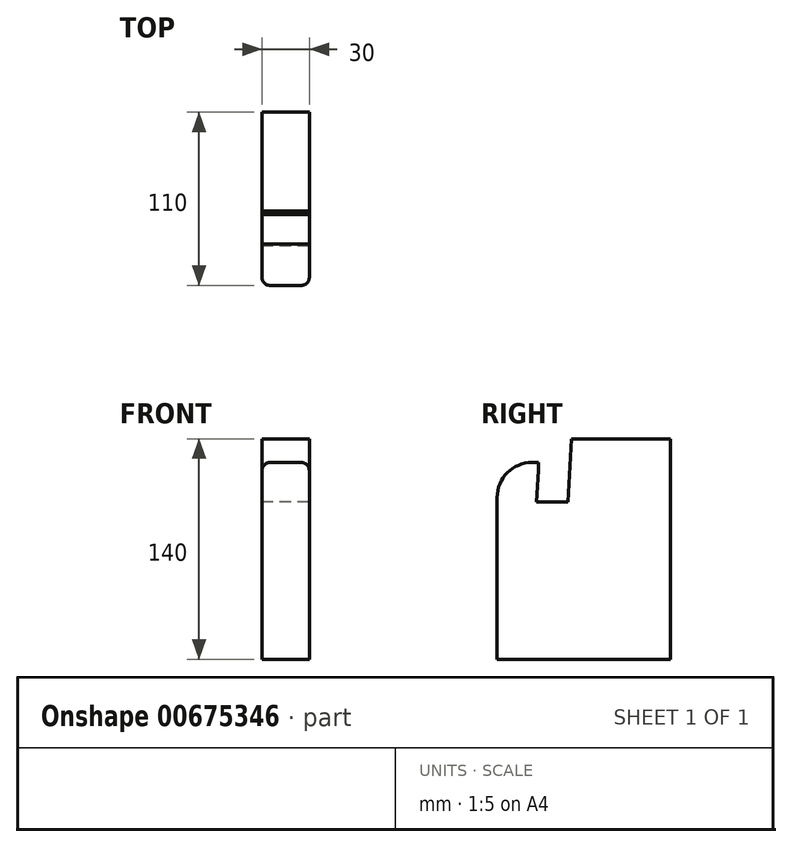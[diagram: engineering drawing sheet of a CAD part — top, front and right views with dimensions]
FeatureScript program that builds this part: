
annotation { "Feature Type Name" : "Feature", "Feature Type Description" : "" }
export const myFeature = defineFeature(function(context is Context, id is Id, definition is map)
    precondition{}
    {
        {
            var Q0;
            Q0=qCreatedBy(makeId("Right.planeOp"),FACE);
            var sketch = newSketch(context, id + "F0", { "sketchPlane" : qUnion([Q0])});
            skLineSegment(sketch, "E0", {"start": v(0, 0) * mm, "end": v(2.1, 39.95) * mm});
            skLineSegment(sketch, "E1", {"start": v(-20, 0) * mm, "end": v(-18.7, 24.97) * mm});
            skLineSegment(sketch, "E2", {"start": v(0, 0) * mm, "end": v(29.88, 570.22) * mm, "construction": true});
            skLineSegment(sketch, "E3", {"start": v(14.94, 285.1) * mm, "end": v(14.94, -214.9) * mm, "construction": true});
            skLineSegment(sketch, "E4", {"start": v(2.1, 39.95) * mm, "end": v(14.94, 39.95) * mm, "construction": true});
            skPoint(sketch, "E4.endSnap0", {"position": v(14.94, 35.1) * mm});
            skLineSegment(sketch, "E5", {"start": v(14.94, 39.95) * mm, "end": v(14.94, -100.05) * mm, "construction": true});
            skLineSegment(sketch, "E6", {"start": v(14.94, -100.05) * mm, "end": v(-45.06, -100.05) * mm, "construction": true});
            skLineSegment(sketch, "E7", {"start": v(14.94, -100.05) * mm, "end": v(64.94, -100.05) * mm, "construction": true});
            skLineSegment(sketch, "E8", {"start": v(64.94, -100.05) * mm, "end": v(64.94, 39.95) * mm});
            skLineSegment(sketch, "E9", {"start": v(64.94, 39.95) * mm, "end": v(2.1, 39.95) * mm});
            skLineSegment(sketch, "E10", {"start": v(-45.06, -100.05) * mm, "end": v(-45.06, 24.97) * mm});
            skLineSegment(sketch, "E11", {"start": v(-45.06, -100.05) * mm, "end": v(64.94, -100.05) * mm});
            skLineSegment(sketch, "E12", {"start": v(-18.7, 24.97) * mm, "end": v(-45.06, 24.97) * mm});
            skLineSegment(sketch, "E13", {"start": v(-20, 0) * mm, "end": v(0, 0) * mm});
            skSolve(sketch);
        }
        {
            var Q0;
            Q0 = qSketchRegion(id + "F0", true);
            extrude(context, id + "F1", {"entities" : qUnion([Q0]), "depth" : 30 * mm, "offsetDistance" : 25 * mm});
        }
        {
            var Q0;
            Q0=makeQuery(id+"F1.opExtrude","SWEPT_EDGE",EDGE,{"disambiguationData":[OSD([sQuery(id+"F0.wireOp",EDGE,"E10"),sQuery(id+"F0.wireOp",EDGE,"E12")])]});
            fillet(context, id + "F2", {"entities" : qUnion([Q0]), "radius" : 22.1 * mm, "tangentPropagation" : true, "allowEdgeOverflow" : false});
        }
        {
            var Q0;
            {var subQ0=sQuery(id+"F0.wireOp",EDGE,"E12");var subQ1=sQuery(id+"F0.wireOp",EDGE,"E10");Q0=makeQuery(id+"F2.opFillet","BLEND_EDGE",EDGE,{"blendedFrom":[makeQuery(id+"F1.opExtrude","SWEPT_EDGE",EDGE,{"disambiguationData":[OSD([subQ1,subQ0])]}),makeQuery(id+"F1.opExtrude","CAP_FACE",FACE,{"disambiguationData":[OSD([sQuery(id+"F0.wireOp",EDGE,"E0"),sQuery(id+"F0.wireOp",EDGE,"E1"),sQuery(id+"F0.wireOp",EDGE,"E8"),sQuery(id+"F0.wireOp",EDGE,"E9"),subQ1,sQuery(id+"F0.wireOp",EDGE,"E11"),subQ0,sQuery(id+"F0.wireOp",EDGE,"E13")])],"isStart":false})],"blendedInto":[makeQuery(id+"F1.opExtrude","CAP_FACE",FACE,{"disambiguationData":[OSD([sQuery(id+"F0.wireOp",EDGE,"E0"),sQuery(id+"F0.wireOp",EDGE,"E1"),sQuery(id+"F0.wireOp",EDGE,"E8"),sQuery(id+"F0.wireOp",EDGE,"E9"),subQ1,sQuery(id+"F0.wireOp",EDGE,"E11"),subQ0,sQuery(id+"F0.wireOp",EDGE,"E13")])],"isStart":false})]});}
            var Q1;
            {var subQ0=sQuery(id+"F0.wireOp",EDGE,"E12");var subQ1=sQuery(id+"F0.wireOp",EDGE,"E10");Q1=makeQuery(id+"F2.opFillet","BLEND_EDGE",EDGE,{"blendedFrom":[makeQuery(id+"F1.opExtrude","SWEPT_EDGE",EDGE,{"disambiguationData":[OSD([subQ1,subQ0])]}),makeQuery(id+"F1.opExtrude","CAP_FACE",FACE,{"disambiguationData":[OSD([sQuery(id+"F0.wireOp",EDGE,"E0"),sQuery(id+"F0.wireOp",EDGE,"E1"),sQuery(id+"F0.wireOp",EDGE,"E8"),sQuery(id+"F0.wireOp",EDGE,"E9"),subQ1,sQuery(id+"F0.wireOp",EDGE,"E11"),subQ0,sQuery(id+"F0.wireOp",EDGE,"E13")])],"isStart":true})],"blendedInto":[makeQuery(id+"F1.opExtrude","CAP_FACE",FACE,{"disambiguationData":[OSD([sQuery(id+"F0.wireOp",EDGE,"E0"),sQuery(id+"F0.wireOp",EDGE,"E1"),sQuery(id+"F0.wireOp",EDGE,"E8"),sQuery(id+"F0.wireOp",EDGE,"E9"),subQ1,sQuery(id+"F0.wireOp",EDGE,"E11"),subQ0,sQuery(id+"F0.wireOp",EDGE,"E13")])],"isStart":true})]});}
            var Q2;
            Q2=makeQuery(id+"F1.opExtrude","CAP_EDGE",EDGE,{"disambiguationData":[OSD([sQuery(id+"F0.wireOp",EDGE,"E12")])],"isStart":false});
            var Q3;
            Q3=makeQuery(id+"F1.opExtrude","CAP_EDGE",EDGE,{"disambiguationData":[OSD([sQuery(id+"F0.wireOp",EDGE,"E12")])],"isStart":true});
            fillet(context, id + "F3", {"entities" : qUnion([Q0, Q1, Q2, Q3]), "radius" : 5 * mm, "tangentPropagation" : true, "allowEdgeOverflow" : false});
        }
    });
